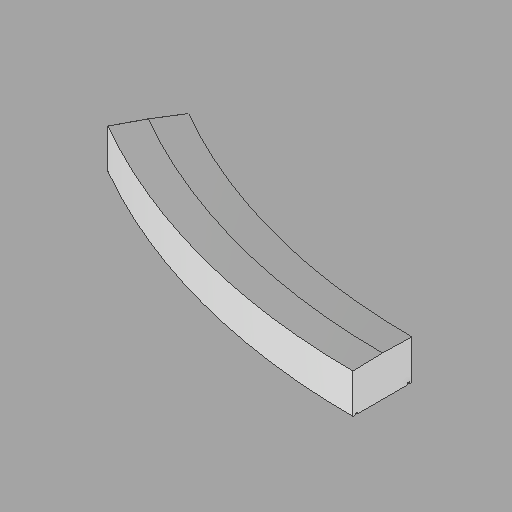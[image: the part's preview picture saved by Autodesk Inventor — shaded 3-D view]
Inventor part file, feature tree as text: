
AUTODESK INVENTOR PART (.ipt)
format: ipt  version: 2022.2 (Build 262287010, 287A)  size: 175,104 bytes
history: native  units: in
note: dims shown in document units (in); Inventor stores cm internally (conversion verified against a paired STEP export)
features: sketch x5, sweep x3, projected_geometry x2, other x1, direct_edit x1, extrude x1, revolve x1
ambient origin geometry x8: Origin, YZ Plane, XZ Plane, XY Plane, X Axis, Y Axis, Z Axis, Center Point
bodies: Solid1 (feature_tree)
feature tree (14):
  other  "Cap (4) (1)"
  direct_edit  "Direct Edit1"
  sketch  "Sketch1"  dims[d0=-0.2061in d1=0.125in]
  sweep  "Sweep1"
  sweep  "Sweep2"
  sweep  "Sweep3"
  extrude  "Extrusion1"  Depth=0.25in
  projected_geometry  "Projected Loop1"
  sketch  "3D Sketch1"
  sketch  "3D Sketch2"
  sketch  "3D Sketch3"
  sketch  "Sketch2"  dims[d2=0.25in d3=0.25in d4=0.25in d5=0.25in d6=0.375in d7=0.375in d8=0.0in d9=0.0in d10=0.0in d11=0.0in d12=0.0in d13=0.0in d14=1.0in d15=0.0in]
  projected_geometry  "Projected Loop2"
  revolve  "Rotate1"  [1 undecoded]
note: 1 required parameter value undecoded (feature->parameter linkage not recoverable at this tier; creation-order binding heuristic only, values carry confidence <= 0.55)
